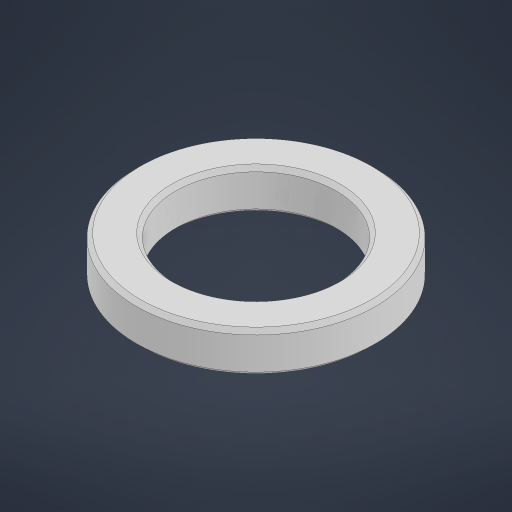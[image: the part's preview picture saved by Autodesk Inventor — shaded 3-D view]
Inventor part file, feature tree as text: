
AUTODESK INVENTOR PART (.ipt)
format: ipt  version: 2023 (Build 270158000, 158)  size: 188,416 bytes
history: native  units: in
note: dims shown in document units (in); Inventor stores cm internally (conversion verified against a paired STEP export)
features: chamfer x1
ambient origin geometry x8: Origin, YZ Plane, XZ Plane, XY Plane, X Axis, Y Axis, Z Axis, Center Point
bodies: Solid1 (feature_tree)
feature tree (1):
  chamfer  "Chamfer1"  [1 undecoded]
note: 1 required parameter value undecoded (feature->parameter linkage not recoverable at this tier; creation-order binding heuristic only, values carry confidence <= 0.55)
